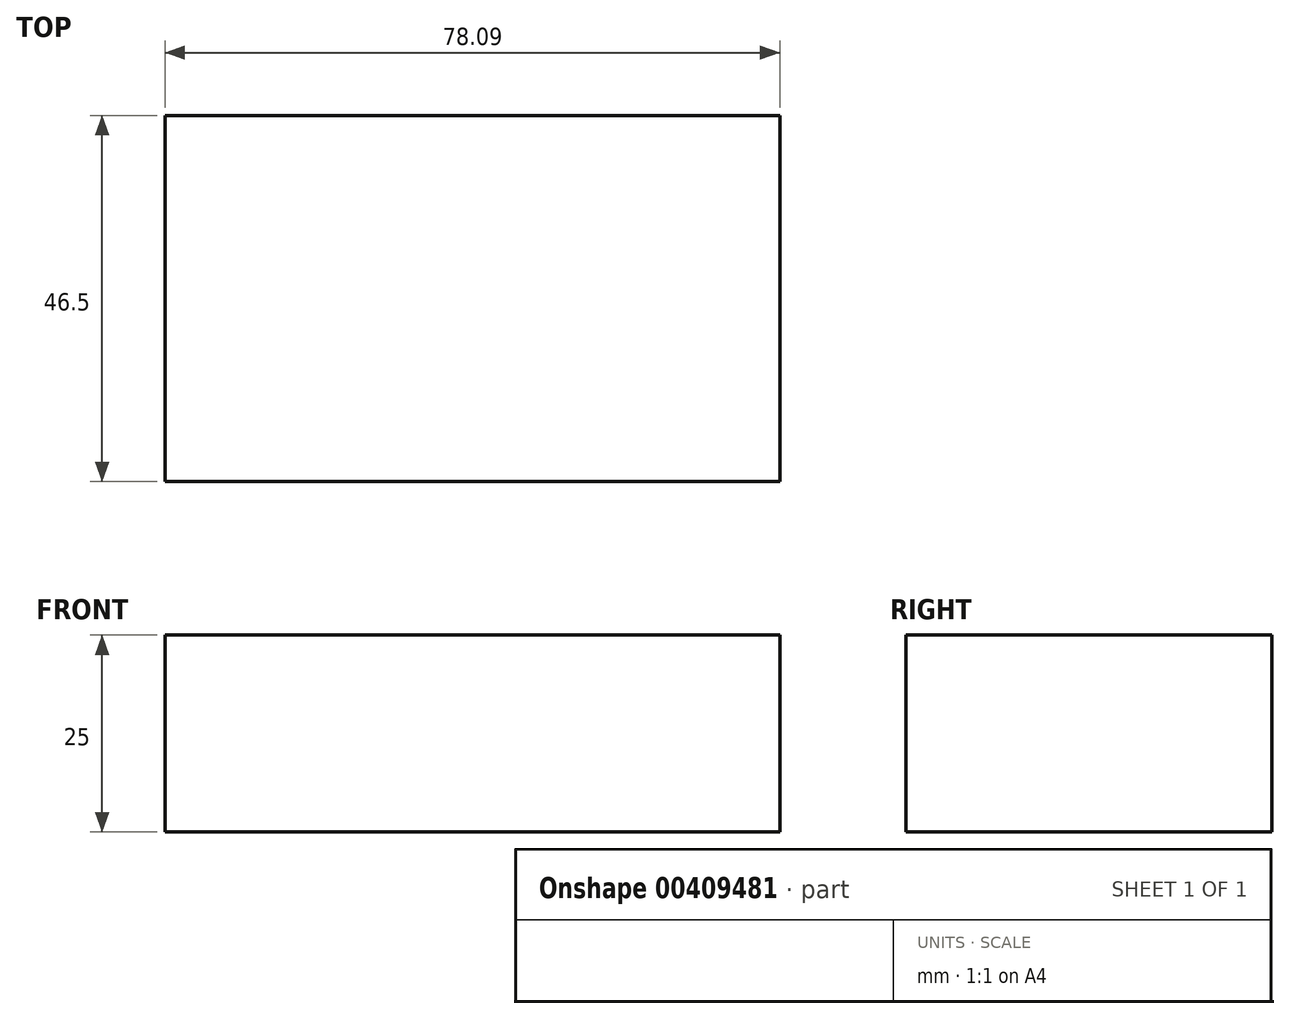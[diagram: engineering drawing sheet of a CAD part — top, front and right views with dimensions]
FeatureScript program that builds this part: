
annotation { "Feature Type Name" : "Feature", "Feature Type Description" : "" }
export const myFeature = defineFeature(function(context is Context, id is Id, definition is map)
    precondition{}
    {
        {
            var Q0;
            Q0=qCreatedBy(makeId("Top.planeOp"),FACE);
            var sketch = newSketch(context, id + "F0", { "sketchPlane" : qUnion([Q0])});
            skLineSegment(sketch, "E0.bottom", {"start": v(43.4, -62.44) * mm, "end": v(-34.7, -62.44) * mm});
            skLineSegment(sketch, "E0.top", {"start": v(43.4, -15.94) * mm, "end": v(-34.7, -15.94) * mm});
            skLineSegment(sketch, "E0.left", {"start": v(43.4, -62.44) * mm, "end": v(43.4, -15.94) * mm});
            skLineSegment(sketch, "E0.right", {"start": v(-34.7, -62.44) * mm, "end": v(-34.7, -15.94) * mm});
            skSolve(sketch);
        }
        {
            var Q0;
            Q0 = qSketchRegion(id + "F0", true);
            extrude(context, id + "F1", {"entities" : qUnion([Q0]), "depth" : 25 * mm});
        }
    });
